# Revit family: Street X1 160LPW
name_source: partatom
category: Осветительные приборы
revit_build: Autodesk Revit 2017 (Build: 20160225_1515(x64)
units: mm (PartAtom-declared; Revit-internal decimal feet)

## family parameters
Всегда вертикально = Да
Источник света = Да
На основе рабочей плоскости = Нет
Общий = Нет
При загрузке вырезать с полостями = Нет
Размер круглого соединителя = Использовать диаметр
Тип детали = Нормальный
Точка расчета площади = Нет

## types (14) — shared parameters
Видимая форма излучения при визуализации = Нет
Изготовитель = LEDEL
Излучение по длине прямоугольника = 362 мм
Излучение по ширине прямоугольника = 173 мм
Классификация нагрузок = Освещение
Комментарии к типоразмеру = Уличные
Светофильтр = 16777215
Смещение цветовой температуры при затухании лампы = <Нет>
Угол наклона = 90.00°

## per-type parameters (varying)
| type | Артикул | Полная установленная мощность | Файл фотометрической сетки |
| Street X1-30-Ш8М-4.0К-05 | X1062 | 30 В·А | Street X1-30-LLI8M-4.0K-05.ies |
| Street X1-120-Ш8М-4.0К-05 | X1036 | 120 В·А | Street X1-120-LLI8M-4.0K-05.ies |
| Street X1-95-Ш8М-4.0К-05 | X1169 | 95 В·А | Street X1-95-LLI8M-4.0K-05.ies |
| Street X1-77-Ш8М-4.0К-05 | X1143 | 77 В·А | Street X1-77-LLI8M-4.0K-05.ies |
| Street X1-60-Ш8М-4.0К-05 | X1118 | 60 В·А | Street X1-60-LLI8M-4.0K-05.ies |
| Street X1-48-Ш8М-4.0К-05 | X1093 | 48 В·А | Street X1-48-LLI8M-4.0K-05.ies |
| Street X1-113-Ш8М-4.0К-05 | X1022 | 113 В·А | Street X1-113-LLI8M-4.0K-05.ies |
| Street X1-30-Ш8М-5.0К-05 | X1056 | 30 В·А | Street X1-30-LLI8M-4.0K-05.ies |
| Street X1-48-Ш8М-5.0К-05 | X1089 | 48 В·А | Street X1-48-LLI8M-4.0K-05.ies |
| Street X1-60-Ш8М-5.0К-05 | X1114 | 60 В·А | Street X1-60-LLI8M-4.0K-05.ies |
| Street X1-77-Ш8М-5.0К-05 | X1139 | 77 В·А | Street X1-77-LLI8M-4.0K-05.ies |
| Street X1-95-Ш8М-5.0К-05 | X1165 | 95 В·А | Street X1-95-LLI8M-4.0K-05.ies |
| Street X1-113-Ш8М-5.0К-05 | X1020 | 113 В·А | Street X1-113-LLI8M-4.0K-05.ies |
| Street X1-120-Ш8М-5.0К-05 | X1032 | 120 В·А | Street X1-120-LLI8M-4.0K-05.ies |
